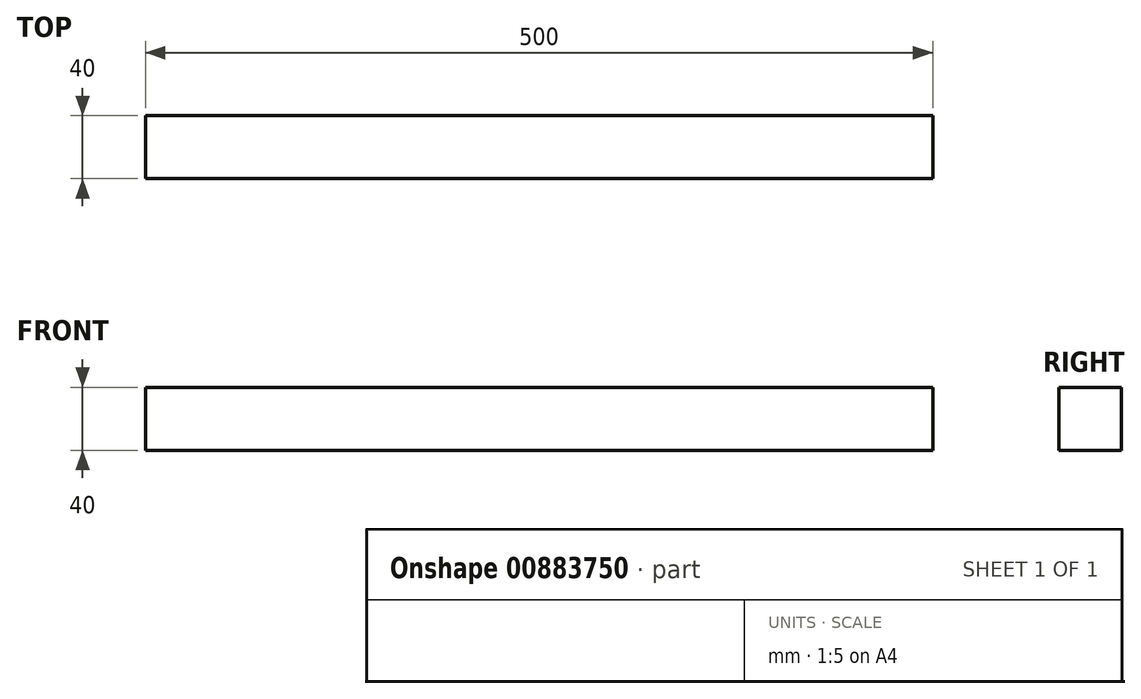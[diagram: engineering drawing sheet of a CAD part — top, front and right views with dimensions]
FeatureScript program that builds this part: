
annotation { "Feature Type Name" : "Feature", "Feature Type Description" : "" }
export const myFeature = defineFeature(function(context is Context, id is Id, definition is map)
    precondition{}
    {
        {
            var Q0;
            Q0=qCreatedBy(makeId("Right.planeOp"),FACE);
            var sketch = newSketch(context, id + "F0", { "sketchPlane" : qUnion([Q0])});
            skLineSegment(sketch, "E0.bottom", {"start": v(118.13, 14.86) * mm, "end": v(78.13, 14.86) * mm});
            skLineSegment(sketch, "E0.top", {"start": v(118.13, 54.86) * mm, "end": v(78.13, 54.86) * mm});
            skLineSegment(sketch, "E0.left", {"start": v(118.13, 14.86) * mm, "end": v(118.13, 54.86) * mm});
            skLineSegment(sketch, "E0.right", {"start": v(78.13, 14.86) * mm, "end": v(78.13, 54.86) * mm});
            skPoint(sketch, "E0.middle", {"position": v(98.13, 34.86) * mm});
            skSolve(sketch);
        }
        {
            var Q0;
            Q0 = qSketchRegion(id + "F0", true);
            extrude(context, id + "F1", {"entities" : qUnion([Q0]), "depth" : 500 * mm, "offsetDistance" : 25 * mm});
        }
    });
